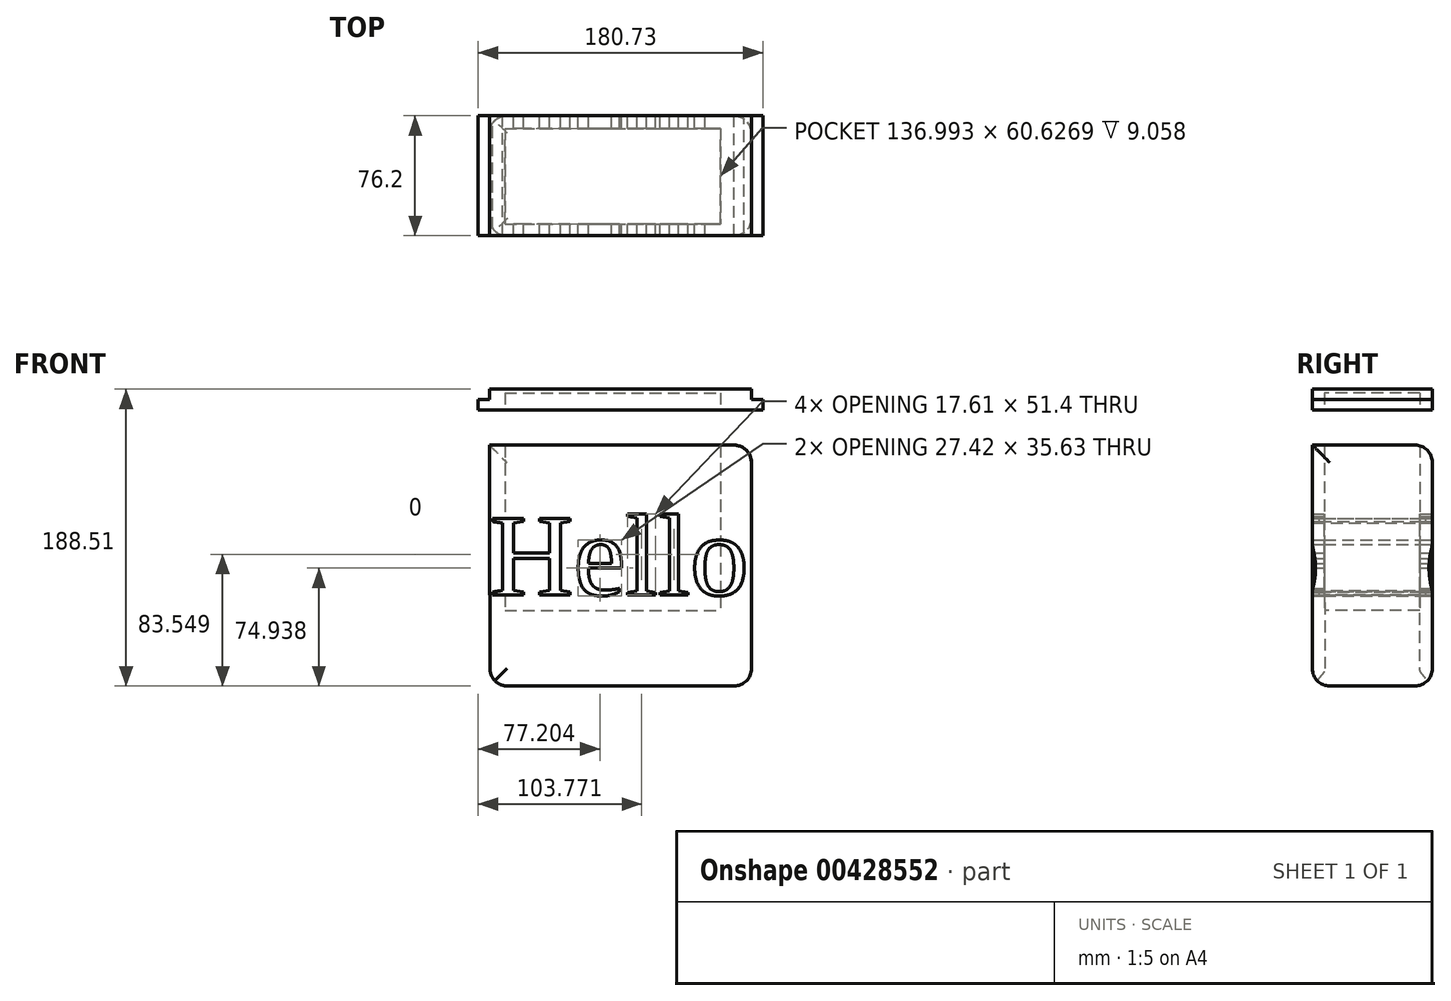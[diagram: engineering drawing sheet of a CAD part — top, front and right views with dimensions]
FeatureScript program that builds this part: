
annotation { "Feature Type Name" : "Feature", "Feature Type Description" : "" }
export const myFeature = defineFeature(function(context is Context, id is Id, definition is map)
    precondition{}
    {
        {
            var Q0;
            Q0=qCreatedBy(makeId("Front.planeOp"),FACE);
            var sketch = newSketch(context, id + "F0", { "sketchPlane" : qUnion([Q0])});
            skLineSegment(sketch, "E0.bottom", {"start": v(-76.01, 0) * mm, "end": v(90, 0) * mm});
            skLineSegment(sketch, "E0.top", {"start": v(-76.01, 9.77) * mm, "end": v(90, 9.77) * mm});
            skLineSegment(sketch, "E0.left", {"start": v(-76.01, 0) * mm, "end": v(-76.01, 9.77) * mm});
            skLineSegment(sketch, "E0.right", {"start": v(90, 0) * mm, "end": v(90, 9.77) * mm});
            skLineSegment(sketch, "E1.top", {"start": v(-76.37, 63.1) * mm, "end": v(90, 63.1) * mm});
            skLineSegment(sketch, "E2.top", {"start": v(-76.37, 9.77) * mm, "end": v(90, 9.77) * mm});
            skLineSegment(sketch, "E2.left", {"start": v(-76.37, 63.1) * mm, "end": v(-76.37, 9.77) * mm});
            skLineSegment(sketch, "E2.right", {"start": v(90, 63.1) * mm, "end": v(90, 9.77) * mm});
            skText(sketch, "E3", { "text": "Hello", "fontName": "Tinos-Regular.ttf"});
            skPoint(sketch, "E4", {"position": v(16.76, -44.03) * mm});
            skPoint(sketch, "E5", {"position": v(-17.26, -17.8) * mm});
            skPoint(sketch, "E6", {"position": v(16.76, -17.47) * mm});
            skPoint(sketch, "E7", {"position": v(28.1, -31.4) * mm});
            skPoint(sketch, "E8", {"position": v(28.1, -34) * mm});
            skPoint(sketch, "E9", {"position": v(25.18, -36.9) * mm});
            skPoint(sketch, "E10", {"position": v(21.94, -41.12) * mm});
            skPoint(sketch, "E11", {"position": v(11.57, -44.03) * mm});
            skPoint(sketch, "E12", {"position": v(4.77, -44.03) * mm});
            skPoint(sketch, "E13", {"position": v(0, -44.03) * mm});
            skPoint(sketch, "E14", {"position": v(8.33, -44.03) * mm});
            skPoint(sketch, "E15", {"position": v(-3.98, -44.03) * mm});
            skPoint(sketch, "E16", {"position": v(-9.16, -44.03) * mm});
            skPoint(sketch, "E17", {"position": v(-13.37, -44.03) * mm});
            skPoint(sketch, "E18", {"position": v(-18.55, -44.03) * mm});
            skPoint(sketch, "E19", {"position": v(-23.1, -41.12) * mm});
            skPoint(sketch, "E20", {"position": v(-28.3, -36.9) * mm});
            skPoint(sketch, "E21", {"position": v(-32.2, -34) * mm});
            skPoint(sketch, "E22", {"position": v(-32.2, -31.4) * mm});
            skLineSegment(sketch, "E23", {"start": v(-76.01, 0) * mm, "end": v(-76.01, -48.08) * mm});
            skLineSegment(sketch, "E24", {"start": v(-76.01, -48.08) * mm, "end": v(90, -48.08) * mm});
            skLineSegment(sketch, "E25", {"start": v(90, -48.08) * mm, "end": v(90, 0) * mm});
            skLineSegment(sketch, "E26", {"start": v(-76.37, 63.1) * mm, "end": v(-76.37, 104.94) * mm});
            skLineSegment(sketch, "E27", {"start": v(-76.37, 104.94) * mm, "end": v(90, 104.94) * mm});
            skLineSegment(sketch, "E28", {"start": v(90, 104.94) * mm, "end": v(90, 63.1) * mm});
            skLineSegment(sketch, "E29", {"start": v(90, 104.94) * mm, "end": v(-76.37, 104.94) * mm});
            skPoint(sketch, "E30.start.orphan", {"position": v(-76.37, 127.21) * mm});
            skPoint(sketch, "E31.orphan", {"position": v(90, 127.21) * mm});
            skPoint(sketch, "E32.right.end.orphan", {"position": v(-88.56, 104.94) * mm});
            skPoint(sketch, "E33.left.end.orphan", {"position": v(-76.37, 153.64) * mm});
            skPoint(sketch, "E33.left.start.orphan", {"position": v(-76.37, 140.43) * mm});
            skPoint(sketch, "E33.right.end.orphan", {"position": v(90, 153.64) * mm});
            skPoint(sketch, "E34.bottom.start.orphan", {"position": v(90, 140.43) * mm});
            skPoint(sketch, "E34.right.end.orphan", {"position": v(102.9, 127.21) * mm});
            skPoint(sketch, "E35.left.start.orphan", {"position": v(-76.37, 209.91) * mm});
            skPoint(sketch, "E35.top.end.orphan", {"position": v(-88.56, 201.38) * mm});
            skPoint(sketch, "E36.top.start.orphan", {"position": v(-76.37, 201.38) * mm});
            skPoint(sketch, "E36.left.start.orphan", {"position": v(-76.37, 218.44) * mm});
            skPoint(sketch, "E37.orphan", {"position": v(90, 218.44) * mm});
            skPoint(sketch, "E38.top.end.orphan", {"position": v(99.04, 201.38) * mm});
            skPoint(sketch, "E36.right.end.orphan", {"position": v(90, 201.38) * mm});
            skPoint(sketch, "E38.left.start.orphan", {"position": v(90, 209.91) * mm});
            skLineSegment(sketch, "E39.bottom", {"start": v(-76.37, 127.21) * mm, "end": v(90, 127.21) * mm});
            skLineSegment(sketch, "E39.top", {"start": v(-76.37, 140.43) * mm, "end": v(90, 140.43) * mm});
            skLineSegment(sketch, "E39.left", {"start": v(-76.37, 127.21) * mm, "end": v(-76.37, 140.43) * mm});
            skLineSegment(sketch, "E39.right", {"start": v(90, 127.21) * mm, "end": v(90, 140.43) * mm});
            skPoint(sketch, "E40.oppositeSnap0", {"position": v(-76.37, 133.82) * mm});
            skLineSegment(sketch, "E40.bottom", {"start": v(-76.37, 127.21) * mm, "end": v(-83.48, 127.21) * mm});
            skLineSegment(sketch, "E40.top", {"start": v(-76.37, 133.82) * mm, "end": v(-83.48, 133.82) * mm});
            skLineSegment(sketch, "E40.left", {"start": v(-76.37, 127.21) * mm, "end": v(-76.37, 133.82) * mm});
            skLineSegment(sketch, "E40.right", {"start": v(-83.48, 127.21) * mm, "end": v(-83.48, 133.82) * mm});
            skLineSegment(sketch, "E41.bottom", {"start": v(90, 133.82) * mm, "end": v(97.25, 133.82) * mm});
            skLineSegment(sketch, "E41.top", {"start": v(90, 127.21) * mm, "end": v(97.25, 127.21) * mm});
            skLineSegment(sketch, "E41.left", {"start": v(90, 133.82) * mm, "end": v(90, 127.21) * mm});
            skLineSegment(sketch, "E41.right", {"start": v(97.25, 133.82) * mm, "end": v(97.25, 127.21) * mm});
            const initialGuessF0  = {"E3": [-0.07637, 0.00977, 1, 0, 0.05333]};
            skSetInitialGuess(sketch, initialGuessF0);
            skSolve(sketch);
        }
        {
            var Q0;
            Q0=makeQuery(id+"F0.imprint","IMPRINT",FACE,{"disambiguationData":[TD([[makeQuery(id+"F0.imprint","IMPRINT",EDGE,{"derivedFrom":sQuery(id+"F0.wireOp",EDGE,"E0.bottom")}),-1.0]])]});
            var Q1;
            Q1=makeQuery(id+"F0.imprint","IMPRINT",FACE,{"disambiguationData":[TD([[makeQuery(id+"F0.imprint","IMPRINT",EDGE,{"derivedFrom":sQuery(id+"F0.wireOp",EDGE,"E1.top")}),1.0]])]});
            var Q2;
            Q2=makeQuery(id+"F0.imprint","IMPRINT",FACE,{"disambiguationData":[TD([[makeQuery(id+"F0.imprint","IMPRINT",EDGE,{"derivedFrom":sQuery(id+"F0.wireOp",EDGE,"VBkPcrcN-UXHz-hrIZ-WuQZ-lOAkPEMZ8GQh.bottom")}),1.0]])]});
            var Q3;
            Q3=makeQuery(id+"F0.imprint","IMPRINT",FACE,{"disambiguationData":[TD([[makeQuery(id+"F0.imprint","IMPRINT",EDGE,{"derivedFrom":sQuery(id+"F0.wireOp",EDGE,"E34.bottom")}),-1.0]])]});
            var Q4;
            Q4=makeQuery(id+"F0.imprint","IMPRINT",FACE,{"disambiguationData":[TD([[makeQuery(id+"F0.imprint","IMPRINT",EDGE,{"derivedFrom":sQuery(id+"F0.wireOp",EDGE,"E33.top")}),-1.0]])]});
            var Q5;
            Q5=makeQuery(id+"F0.imprint","IMPRINT",FACE,{"disambiguationData":[TD([[makeQuery(id+"F0.imprint","IMPRINT",EDGE,{"derivedFrom":sQuery(id+"F0.wireOp",EDGE,"E1.top")}),-1.0]])]});
            var Q6;
            Q6=makeQuery(id+"F0.imprint","IMPRINT",FACE,{"disambiguationData":[TD([[makeQuery(id+"F0.imprint","IMPRINT",EDGE,{"derivedFrom":sQuery(id+"F0.wireOp",EDGE,"E0.bottom")}),1.0]])]});
            var Q7;
            {var subQ0=sQuery(id+"F0.wireOp",EDGE,"E3.sketch_text.stroke-20");Q7=makeQuery(id+"F0.imprint","IMPRINT",FACE,{"disambiguationData":[TD([[makeQuery(id+"F0.imprint","IMPRINT",EDGE,{"derivedFrom":subQ0}),1.0]])]});}
            var Q8;
            Q8=makeQuery(id+"F0.imprint","IMPRINT",FACE,{"disambiguationData":[TD([[makeQuery(id+"F0.imprint","IMPRINT",EDGE,{"derivedFrom":sQuery(id+"F0.wireOp",EDGE,"E3.sketch_text.stroke-44")}),1.0]])]});
            var Q9;
            Q9=makeQuery(id+"F0.imprint","IMPRINT",FACE,{"disambiguationData":[TD([[makeQuery(id+"F0.imprint","IMPRINT",EDGE,{"derivedFrom":sQuery(id+"F0.wireOp",EDGE,"E3.sketch_text.stroke-76")}),1.0]])]});
            var Q10;
            Q10=makeQuery(id+"F0.imprint","IMPRINT",FACE,{"disambiguationData":[TD([[makeQuery(id+"F0.imprint","IMPRINT",EDGE,{"derivedFrom":sQuery(id+"F0.wireOp",EDGE,"E36.bottom")}),-1.0]])]});
            var Q11;
            Q11=makeQuery(id+"F0.imprint","IMPRINT",FACE,{"disambiguationData":[TD([[makeQuery(id+"F0.imprint","IMPRINT",EDGE,{"derivedFrom":sQuery(id+"F0.wireOp",EDGE,"E35.bottom")}),1.0]])]});
            var Q12;
            Q12=makeQuery(id+"F0.imprint","IMPRINT",FACE,{"disambiguationData":[TD([[makeQuery(id+"F0.imprint","IMPRINT",EDGE,{"derivedFrom":sQuery(id+"F0.wireOp",EDGE,"E38.bottom")}),-1.0]])]});
            var Q13;
            Q13=makeQuery(id+"F0.imprint","IMPRINT",FACE,{"disambiguationData":[TD([[makeQuery(id+"F0.imprint","IMPRINT",EDGE,{"derivedFrom":sQuery(id+"F0.wireOp",EDGE,"E40.bottom")}),-1.0]])]});
            var Q14;
            Q14=makeQuery(id+"F0.imprint","IMPRINT",FACE,{"disambiguationData":[TD([[makeQuery(id+"F0.imprint","IMPRINT",EDGE,{"derivedFrom":sQuery(id+"F0.wireOp",EDGE,"E39.bottom")}),1.0]])]});
            var Q15;
            Q15=makeQuery(id+"F0.imprint","IMPRINT",FACE,{"disambiguationData":[TD([[makeQuery(id+"F0.imprint","IMPRINT",EDGE,{"derivedFrom":sQuery(id+"F0.wireOp",EDGE,"E41.bottom")}),-1.0]])]});
            extrude(context, id + "F1", {"entities" : qUnion([Q0, Q1, Q2, Q3, Q4, Q5, Q6, Q7, Q8, Q9, Q10, Q11, Q12, Q13, Q14, Q15]), "depth" : 76.2 * mm});
        }
        {
            var Q0;
            Q0=makeQuery(id+"F1.opExtrude","CAP_EDGE",EDGE,{"disambiguationData":[OSD([sQuery(id+"F0.wireOp",EDGE,"E27")])],"isStart":true});
            var Q1;
            Q1=makeQuery(id+"F1.opExtrude","SWEPT_EDGE",EDGE,{"disambiguationData":[OSD([sQuery(id+"F0.wireOp",EDGE,"E27"),sQuery(id+"F0.wireOp",EDGE,"E28")])]});
            var Q2;
            Q2=makeQuery(id+"F1.opExtrude","CAP_EDGE",EDGE,{"disambiguationData":[OSD([sQuery(id+"F0.wireOp",EDGE,"E0.right"),sQuery(id+"F0.wireOp",EDGE,"E2.right"),sQuery(id+"F0.wireOp",EDGE,"E25"),sQuery(id+"F0.wireOp",EDGE,"E28")])],"isStart":true});
            var Q3;
            Q3=makeQuery(id+"F1.opExtrude","CAP_EDGE",EDGE,{"disambiguationData":[OSD([sQuery(id+"F0.wireOp",EDGE,"E0.right"),sQuery(id+"F0.wireOp",EDGE,"E2.right"),sQuery(id+"F0.wireOp",EDGE,"E25"),sQuery(id+"F0.wireOp",EDGE,"E28")])],"isStart":false});
            var Q4;
            Q4=makeQuery(id+"F1.opExtrude","CAP_EDGE",EDGE,{"disambiguationData":[OSD([sQuery(id+"F0.wireOp",EDGE,"E2.left"),sQuery(id+"F0.wireOp",EDGE,"E26")])],"isStart":false});
            var Q5;
            Q5=makeQuery(id+"F1.opExtrude","CAP_EDGE",EDGE,{"disambiguationData":[OSD([sQuery(id+"F0.wireOp",EDGE,"E24")])],"isStart":false});
            var Q6;
            Q6=makeQuery(id+"F1.opExtrude","SWEPT_EDGE",EDGE,{"disambiguationData":[OSD([sQuery(id+"F0.wireOp",EDGE,"E24"),sQuery(id+"F0.wireOp",EDGE,"E25")])]});
            var Q7;
            Q7=makeQuery(id+"F1.opExtrude","CAP_EDGE",EDGE,{"disambiguationData":[OSD([sQuery(id+"F0.wireOp",EDGE,"E2.left"),sQuery(id+"F0.wireOp",EDGE,"E26")])],"isStart":true});
            var Q8;
            Q8=makeQuery(id+"F1.opExtrude","SWEPT_EDGE",EDGE,{"disambiguationData":[OSD([sQuery(id+"F0.wireOp",EDGE,"E23"),sQuery(id+"F0.wireOp",EDGE,"E24")])]});
            var Q9;
            Q9=makeQuery(id+"F1.opExtrude","CAP_EDGE",EDGE,{"disambiguationData":[OSD([sQuery(id+"F0.wireOp",EDGE,"E24")])],"isStart":true});
            fillet(context, id + "F2", {"entities" : qUnion([Q0, Q1, Q2, Q3, Q4, Q5, Q6, Q7, Q8, Q9]), "radius" : 11.04 * mm, "tangentPropagation" : true, "allowEdgeOverflow" : false});
        }
        {
            var Q0;
            Q0=qCreatedBy(makeId("Top.planeOp"),FACE);
            var sketch = newSketch(context, id + "F3", { "sketchPlane" : qUnion([Q0])});
            skLineSegment(sketch, "E42.bottom", {"start": v(-66.57, -8.02) * mm, "end": v(70.42, -8.02) * mm});
            skLineSegment(sketch, "E42.top", {"start": v(-66.57, -68.64) * mm, "end": v(70.42, -68.64) * mm});
            skLineSegment(sketch, "E42.left", {"start": v(-66.57, -8.02) * mm, "end": v(-66.57, -68.64) * mm});
            skLineSegment(sketch, "E42.right", {"start": v(70.42, -8.02) * mm, "end": v(70.42, -68.64) * mm});
            skLineSegment(sketch, "E43", {"start": v(70.42, -68.64) * mm, "end": v(70.42, -8.02) * mm});
            skLineSegment(sketch, "E44", {"start": v(70.42, -68.64) * mm, "end": v(-66.57, -68.64) * mm});
            skLineSegment(sketch, "E45", {"start": v(-66.57, -68.64) * mm, "end": v(-66.57, -8.02) * mm});
            skSolve(sketch);
        }
        {
            var Q0;
            Q0 = qSketchRegion(id + "F3", true);
            extrude(context, id + "F4", {"entities" : qUnion([Q0]), "operationType" : NewBodyOperationType.REMOVE, "depth" : 138.18 * mm});
        }
    });
